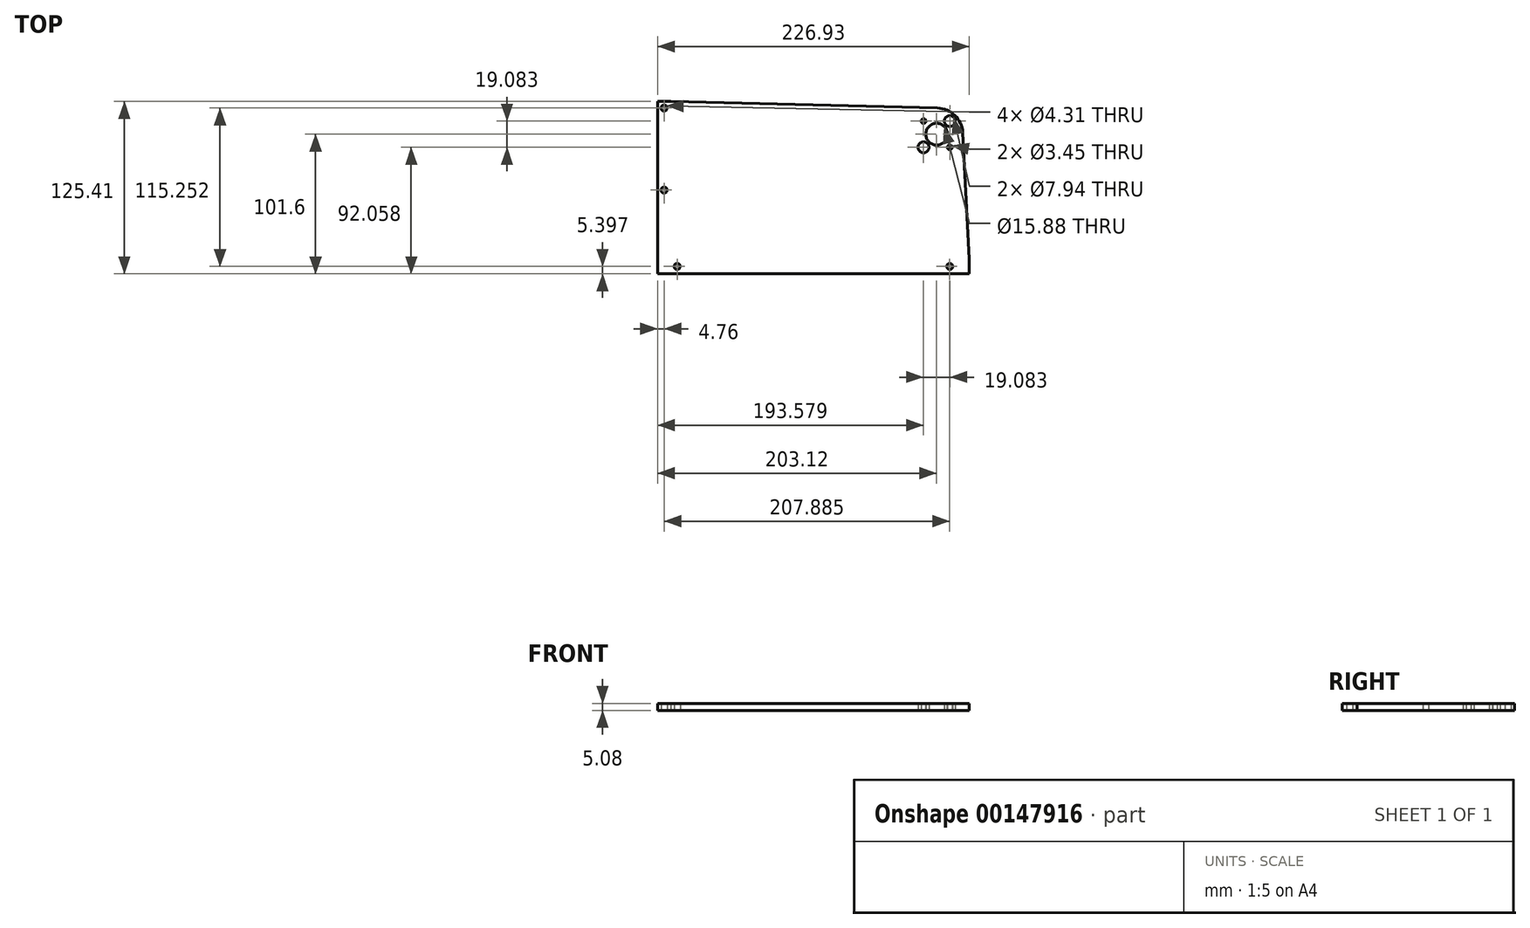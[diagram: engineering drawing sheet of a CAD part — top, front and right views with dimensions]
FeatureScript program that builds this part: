
annotation { "Feature Type Name" : "Feature", "Feature Type Description" : "" }
export const myFeature = defineFeature(function(context is Context, id is Id, definition is map)
    precondition{}
    {
        {
            var Q0;
            Q0=qCreatedBy(makeId("Top.planeOp"),FACE);
            var sketch = newSketch(context, id + "F0", { "sketchPlane" : qUnion([Q0])});
            skCircle(sketch, "E0", {"center": v(0, 0) * mm, "radius": 7.94 * mm});
            skCircle(sketch, "E1", {"center": v(-9.54, 9.54) * mm, "radius": 5.56 * mm, "construction": true});
            skCircle(sketch, "E2", {"center": v(-9.54, 9.54) * mm, "radius": 1.73 * mm});
            skCircle(sketch, "E3", {"center": v(9.54, -9.54) * mm, "radius": 1.73 * mm});
            skLineSegment(sketch, "E4.bottom", {"start": v(-193.6, 23.81) * mm, "end": v(0.47, 19.04) * mm});
            skLineSegment(sketch, "E4.top", {"start": v(-203.12, -101.6) * mm, "end": v(23.81, -101.6) * mm});
            skLineSegment(sketch, "E4.left", {"start": v(-203.12, 23.81) * mm, "end": v(-203.12, -101.6) * mm});
            skLineSegment(sketch, "E5.bottom", {"start": v(-9.54, 9.54) * mm, "end": v(9.54, 9.54) * mm, "construction": true});
            skLineSegment(sketch, "E5.top", {"start": v(-9.54, -9.54) * mm, "end": v(9.54, -9.54) * mm, "construction": true});
            skLineSegment(sketch, "E5.left", {"start": v(-9.54, 9.54) * mm, "end": v(-9.54, -9.54) * mm, "construction": true});
            skLineSegment(sketch, "E5.right", {"start": v(9.54, 9.54) * mm, "end": v(9.54, -9.54) * mm, "construction": true});
            skCircle(sketch, "E6", {"center": v(-9.54, -9.54) * mm, "radius": 3.97 * mm});
            skCircle(sketch, "E7", {"center": v(9.54, 9.54) * mm, "radius": 3.97 * mm});
            skArc(sketch, "E8", {"start": v(19.02, 1) * mm, "mid": v(13.28, 13.65) * mm, "end": v(0.47, 19.04) * mm});
            skLineSegment(sketch, "E9", {"start": v(23.81, -101.6) * mm, "end": v(23.81, -90.8) * mm});
            skLineSegment(sketch, "E10", {"start": v(23.81, -90.8) * mm, "end": v(19.02, 1) * mm});
            skLineSegment(sketch, "E11", {"start": v(0, 0) * mm, "end": v(0, -101.6) * mm, "construction": true});
            skLineSegment(sketch, "E12", {"start": v(23.81, -96.2) * mm, "end": v(9.53, -96.2) * mm, "construction": true});
            skCircle(sketch, "E13", {"center": v(9.53, -96.2) * mm, "radius": 2.15 * mm});
            skLineSegment(sketch, "E14", {"start": v(23.81, -90.8) * mm, "end": v(0, -90.8) * mm, "construction": true});
            skLineSegment(sketch, "E15", {"start": v(-203.12, 23.81) * mm, "end": v(-193.6, 23.81) * mm});
            skLineSegment(sketch, "E16", {"start": v(-198.36, 23.81) * mm, "end": v(-198.36, 19.05) * mm, "construction": true});
            skLineSegment(sketch, "E17", {"start": v(-203.12, -96.2) * mm, "end": v(-188.83, -96.2) * mm, "construction": true});
            skCircle(sketch, "E18", {"center": v(-188.83, -96.2) * mm, "radius": 2.15 * mm});
            skCircle(sketch, "E19", {"center": v(-198.36, 19.05) * mm, "radius": 2.15 * mm});
            skLineSegment(sketch, "E20", {"start": v(0, 0) * mm, "end": v(-198.36, 0) * mm, "construction": true});
            skLineSegment(sketch, "E21", {"start": v(-198.36, 0) * mm, "end": v(-198.36, 19.05) * mm, "construction": true});
            skLineSegment(sketch, "E22", {"start": v(-198.36, 0) * mm, "end": v(-198.36, -40.65) * mm, "construction": true});
            skLineSegment(sketch, "E23", {"start": v(-198.36, -40.65) * mm, "end": v(-198.36, -96.2) * mm, "construction": true});
            skCircle(sketch, "E24", {"center": v(-198.36, -40.65) * mm, "radius": 2.15 * mm});
            skSolve(sketch);
        }
        {
            var Q0;
            Q0=qSketchRegion(id+"F0",true);
            extrude(context, id + "F1", {"entities" : qUnion([Q0]), "depth" : 5.08 * mm});
        }
    });
